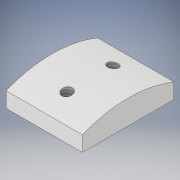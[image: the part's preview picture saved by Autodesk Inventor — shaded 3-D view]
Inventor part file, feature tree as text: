
AUTODESK INVENTOR PART (.ipt)
format: ipt  version: 2017 (Build 210142000, 142)  size: 117,248 bytes
history: native  units: in
note: dims shown in document units (in); Inventor stores cm internally (conversion verified against a paired STEP export)
features: sketch x2, extrude x1, hole x1, projected_geometry x1
ambient origin geometry x8: Origin, YZ Plane, XZ Plane, XY Plane, X Axis, Y Axis, Z Axis, Center Point
bodies: Solid1 (feature_tree)
feature tree (5):
  extrude  "Extrusion1"  Depth=0.125in
  hole  "Hole1"  [1 undecoded]
  sketch  "Sketch1"  dims[d0=0.75in d4=0.125in]
  sketch  "Sketch2"  dims[d6=1.0in d7=0.75in d8=0.625in d9=0.0in d10=0.625in d11=0.3125in d12=0.3125in d13=0.375in d14=0.75in d15=0.1875in d16=0.085in d17=0.224in d18=0.375in d19=0.25in d20=0.5635in d21=0.25in d22=0.8108in d23=0.125in]
  projected_geometry  "Projected Loop1"
note: 1 required parameter value undecoded (feature->parameter linkage not recoverable at this tier; creation-order binding heuristic only, values carry confidence <= 0.55)
